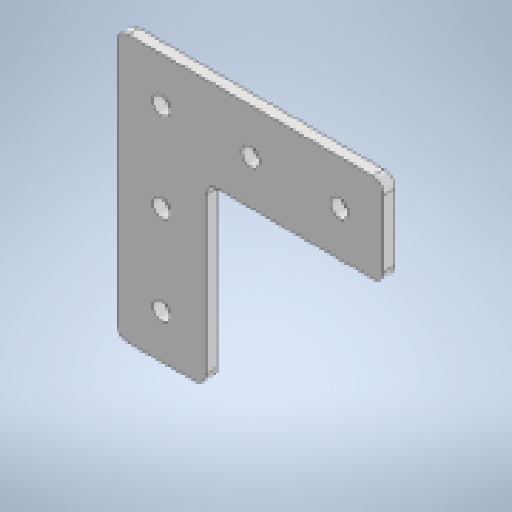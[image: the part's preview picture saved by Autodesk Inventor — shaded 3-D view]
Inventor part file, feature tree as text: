
AUTODESK INVENTOR PART (.ipt)
format: ipt  version: 2024 (Build 280153000, 153)  size: 160,768 bytes
history: native  units: in
note: dims shown in document units (in); Inventor stores cm internally (conversion verified against a paired STEP export)
features: extrude x1, fillet x1
ambient origin geometry x8: Origin, YZ Plane, XZ Plane, XY Plane, X Axis, Y Axis, Z Axis, Center Point
bodies: Solid1 (feature_tree)
feature tree (2):
  extrude  "Extrusion1"  Depth=3.0in
  fillet  "Fillet1"  Radius=1.0in
